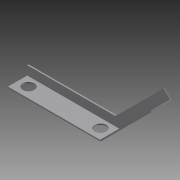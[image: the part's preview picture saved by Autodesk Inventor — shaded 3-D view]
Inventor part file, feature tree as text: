
AUTODESK INVENTOR PART (.ipt)
format: ipt  version: 2012 (Build 160160000, 160)  size: 91,648 bytes
history: native  units: in
note: dims shown in document units (in); Inventor stores cm internally (conversion verified against a paired STEP export)
features: other x3, sketch x2
ambient origin geometry x8: Origin, YZ Plane, XZ Plane, XY Plane, X Axis, Y Axis, Z Axis, Center Point
bodies: Solid1 (feature_tree)
feature tree (5):
  other  "8 ball bottom 1 by 2 L.ipt"
  other  "Solid1::8 ball bottom 1 by 2 L.ipt"
  sketch  "Sketch1"  dims[d0=0.3937in]
  sketch  "Sketch2"
  other  "TaggingFeature1"
